# Revit family: Elite_OX_Standard
name_source: partatom
category: Windows
revit_build: Autodesk Revit 2014 (Build: 20130308_1515(x64)
units: mm (PartAtom-declared; Revit-internal decimal feet)

## types (108) — shared parameters
Centered In Wall = Yes
Custom Sash Width Left = 600 mm
Default Sill Height = 800 mm
Description = Elite Sliding Window OX
Equal Sash Width = Yes
Frame Thickness = 70 mm
Glass Type = Glass
Limit Sash Height Max = 1800 mm  [stored 5.90551 ft]
Limit Sash Height Min = 300 mm
Limit Sash Width Max = 1500 mm  [stored 4.92126 ft]
Limit Sash Width Min = 300 mm
Limit Window Height Max = 1883 mm
Limit Window Height Min = 383 mm  [stored 1.25656 ft]
Limit Window Width Min = 594 mm
Manufacturer = Crealco
Model = Elite Sliding Window OX
Rough Width = 3 mm  [stored 0.00984252 ft]
Sash Frame Seal = 3 mm  [stored 0.00984252 ft]
Sash Side Spacing = 1 mm  [stored 0.00328084 ft]
Wall Closure = By host
zero-valued in all types: Custom Frame Offset From Exterior

## per-type parameters (varying)
| type | Area Left Sash Glazing | Area Right Sash Glazing | Custom Windload | Custom Window Height | Custom Window Width | Glazing Thickness | Height | Inside Heavy Duty Interlocker | Interlocker Configuration | Limit Sash Width Left Max | Limit Sash Width Left Min | Limit Window Width Max | Max Pane Area | Outside Heavy Duty Interlocker | Sash Height | Sash Width Left | Sash Width Right | Standard Interlocker | Width | Windload Design |
| Elite-0906OX-1000Pa | 0.16 m² | 0.16 m² | 1000 mm  [stored 3.28084 ft] | 590 mm  [stored 1.9357 ft] | 890 mm  [stored 2.91995 ft] | 4 mm  [stored 0.0131234 ft] | 590 mm  [stored 1.9357 ft] | No | 0 mm  [stored 0 ft] | 596 mm | 300 mm | 2994 mm | 0.16 m² | No | 507 mm | 448 mm | 448 mm | Yes | 890 mm  [stored 2.91995 ft] | 1000 mm  [stored 3.28084 ft] |
| Elite-0906OX-1500Pa | 0.16 m² | 0.16 m² | 1500 mm  [stored 4.92126 ft] | 590 mm  [stored 1.9357 ft] | 890 mm  [stored 2.91995 ft] | 4 mm  [stored 0.0131234 ft] | 590 mm  [stored 1.9357 ft] | No | 0 mm  [stored 0 ft] | 596 mm | 300 mm | 2994 mm | 0.16 m² | No | 507 mm | 448 mm | 448 mm | Yes | 890 mm  [stored 2.91995 ft] | 1500 mm  [stored 4.92126 ft] |
| Elite-0906OX-2000Pa | 0.16 m² | 0.16 m² | 2000 mm  [stored 6.56168 ft] | 590 mm  [stored 1.9357 ft] | 890 mm  [stored 2.91995 ft] | 4 mm  [stored 0.0131234 ft] | 590 mm  [stored 1.9357 ft] | No | 0 mm  [stored 0 ft] | 596 mm | 300 mm | 2994 mm | 0.16 m² | No | 507 mm | 448 mm | 448 mm | Yes | 890 mm  [stored 2.91995 ft] | 2000 mm  [stored 6.56168 ft] |
| Elite-1206OX-1000Pa | 0.22 m² | 0.22 m² | 1000 mm  [stored 3.28084 ft] | 590 mm  [stored 1.9357 ft] | 1190 mm  [stored 3.9042 ft] | 4 mm  [stored 0.0131234 ft] | 590 mm  [stored 1.9357 ft] | No | 0 mm  [stored 0 ft] | 896 mm | 300 mm | 2994 mm | 0.22 m² | No | 507 mm | 598 mm | 598 mm | Yes | 1190 mm  [stored 3.9042 ft] | 1000 mm  [stored 3.28084 ft] |
| Elite-1206OX-1500Pa | 0.22 m² | 0.22 m² | 1500 mm  [stored 4.92126 ft] | 590 mm  [stored 1.9357 ft] | 1190 mm  [stored 3.9042 ft] | 4 mm  [stored 0.0131234 ft] | 590 mm  [stored 1.9357 ft] | No | 0 mm  [stored 0 ft] | 896 mm | 300 mm | 2994 mm | 0.22 m² | No | 507 mm | 598 mm | 598 mm | Yes | 1190 mm  [stored 3.9042 ft] | 1500 mm  [stored 4.92126 ft] |
| Elite-1206OX-2000Pa | 0.22 m² | 0.22 m² | 2000 mm  [stored 6.56168 ft] | 590 mm  [stored 1.9357 ft] | 1190 mm  [stored 3.9042 ft] | 4 mm  [stored 0.0131234 ft] | 590 mm  [stored 1.9357 ft] | No | 0 mm  [stored 0 ft] | 896 mm | 300 mm | 2994 mm | 0.22 m² | No | 507 mm | 598 mm | 598 mm | Yes | 1190 mm  [stored 3.9042 ft] | 2000 mm  [stored 6.56168 ft] |
| Elite-1506OX-1000Pa | 0.28 m² | 0.28 m² | 1000 mm  [stored 3.28084 ft] | 590 mm  [stored 1.9357 ft] | 1490 mm  [stored 4.88845 ft] | 4 mm  [stored 0.0131234 ft] | 590 mm  [stored 1.9357 ft] | No | 0 mm  [stored 0 ft] | 1196 mm | 300 mm | 2994 mm | 0.28 m² | No | 507 mm | 748 mm | 748 mm | Yes | 1490 mm  [stored 4.88845 ft] | 1000 mm  [stored 3.28084 ft] |
| Elite-1506OX-1500Pa | 0.28 m² | 0.28 m² | 1500 mm  [stored 4.92126 ft] | 590 mm  [stored 1.9357 ft] | 1490 mm  [stored 4.88845 ft] | 4 mm  [stored 0.0131234 ft] | 590 mm  [stored 1.9357 ft] | No | 0 mm  [stored 0 ft] | 1196 mm | 300 mm | 2994 mm | 0.28 m² | No | 507 mm | 748 mm | 748 mm | Yes | 1490 mm  [stored 4.88845 ft] | 1500 mm  [stored 4.92126 ft] |
| Elite-1506OX-2000Pa | 0.28 m² | 0.28 m² | 2000 mm  [stored 6.56168 ft] | 590 mm  [stored 1.9357 ft] | 1490 mm  [stored 4.88845 ft] | 4 mm  [stored 0.0131234 ft] | 590 mm  [stored 1.9357 ft] | No | 0 mm  [stored 0 ft] | 1196 mm | 300 mm | 2994 mm | 0.28 m² | No | 507 mm | 748 mm | 748 mm | Yes | 1490 mm  [stored 4.88845 ft] | 2000 mm  [stored 6.56168 ft] |
| Elite-1806OX-1000Pa | 0.35 m² | 0.35 m² | 1000 mm  [stored 3.28084 ft] | 590 mm  [stored 1.9357 ft] | 1790 mm  [stored 5.8727 ft] | 4 mm  [stored 0.0131234 ft] | 590 mm  [stored 1.9357 ft] | No | 0 mm  [stored 0 ft] | 1496 mm | 300 mm | 2994 mm | 0.35 m² | No | 507 mm | 898 mm | 898 mm | Yes | 1790 mm  [stored 5.8727 ft] | 1000 mm  [stored 3.28084 ft] |
| Elite-1806OX-1500Pa | 0.35 m² | 0.35 m² | 1500 mm  [stored 4.92126 ft] | 590 mm  [stored 1.9357 ft] | 1790 mm  [stored 5.8727 ft] | 4 mm  [stored 0.0131234 ft] | 590 mm  [stored 1.9357 ft] | No | 0 mm  [stored 0 ft] | 1496 mm | 300 mm | 2994 mm | 0.35 m² | No | 507 mm | 898 mm | 898 mm | Yes | 1790 mm  [stored 5.8727 ft] | 1500 mm  [stored 4.92126 ft] |
| Elite-1806OX-2000Pa | 0.35 m² | 0.35 m² | 2000 mm  [stored 6.56168 ft] | 590 mm  [stored 1.9357 ft] | 1790 mm  [stored 5.8727 ft] | 4 mm  [stored 0.0131234 ft] | 590 mm  [stored 1.9357 ft] | No | 0 mm  [stored 0 ft] | 1496 mm | 300 mm | 2994 mm | 0.35 m² | No | 507 mm | 898 mm | 898 mm | Yes | 1790 mm  [stored 5.8727 ft] | 2000 mm  [stored 6.56168 ft] |
| Elite-2106OX-1000Pa | 0.41 m² | 0.41 m² | 1000 mm  [stored 3.28084 ft] | 590 mm  [stored 1.9357 ft] | 2090 mm | 4 mm  [stored 0.0131234 ft] | 590 mm  [stored 1.9357 ft] | No | 0 mm  [stored 0 ft] | 1500 mm  [stored 4.92126 ft] | 596 mm | 2994 mm | 0.41 m² | No | 507 mm | 1048 mm | 1048 mm | Yes | 2090 mm | 1000 mm  [stored 3.28084 ft] |
| Elite-2106OX-1500Pa | 0.41 m² | 0.41 m² | 1500 mm  [stored 4.92126 ft] | 590 mm  [stored 1.9357 ft] | 2090 mm | 4 mm  [stored 0.0131234 ft] | 590 mm  [stored 1.9357 ft] | No | 0 mm  [stored 0 ft] | 1500 mm  [stored 4.92126 ft] | 596 mm | 2994 mm | 0.41 m² | No | 507 mm | 1048 mm | 1048 mm | Yes | 2090 mm | 1500 mm  [stored 4.92126 ft] |
| Elite-2106OX-2000Pa | 0.41 m² | 0.41 m² | 2000 mm  [stored 6.56168 ft] | 590 mm  [stored 1.9357 ft] | 2090 mm | 4 mm  [stored 0.0131234 ft] | 590 mm  [stored 1.9357 ft] | No | 0 mm  [stored 0 ft] | 1500 mm  [stored 4.92126 ft] | 596 mm | 2994 mm | 0.41 m² | No | 507 mm | 1048 mm | 1048 mm | Yes | 2090 mm | 2000 mm  [stored 6.56168 ft] |
| Elite-2406OX-1000Pa | 0.47 m² | 0.47 m² | 1000 mm  [stored 3.28084 ft] | 590 mm  [stored 1.9357 ft] | 2390 mm | 4 mm  [stored 0.0131234 ft] | 590 mm  [stored 1.9357 ft] | No | 0 mm  [stored 0 ft] | 1500 mm  [stored 4.92126 ft] | 896 mm | 2994 mm | 0.47 m² | No | 507 mm | 1198 mm | 1198 mm | Yes | 2390 mm | 1000 mm  [stored 3.28084 ft] |
| Elite-2406OX-1500Pa | 0.47 m² | 0.47 m² | 1500 mm  [stored 4.92126 ft] | 590 mm  [stored 1.9357 ft] | 2390 mm | 4 mm  [stored 0.0131234 ft] | 590 mm  [stored 1.9357 ft] | No | 0 mm  [stored 0 ft] | 1500 mm  [stored 4.92126 ft] | 896 mm | 2994 mm | 0.47 m² | No | 507 mm | 1198 mm | 1198 mm | Yes | 2390 mm | 1500 mm  [stored 4.92126 ft] |
| Elite-2406OX-2000Pa | 0.47 m² | 0.47 m² | 2000 mm  [stored 6.56168 ft] | 590 mm  [stored 1.9357 ft] | 2390 mm | 4 mm  [stored 0.0131234 ft] | 590 mm  [stored 1.9357 ft] | No | 0 mm  [stored 0 ft] | 1500 mm  [stored 4.92126 ft] | 896 mm | 2994 mm | 0.47 m² | No | 507 mm | 1198 mm | 1198 mm | Yes | 2390 mm | 2000 mm  [stored 6.56168 ft] |
| Elite-2706OX-1000Pa | 0.53 m² | 0.53 m² | 1000 mm  [stored 3.28084 ft] | 590 mm  [stored 1.9357 ft] | 2690 mm | 4 mm  [stored 0.0131234 ft] | 590 mm  [stored 1.9357 ft] | No | 0 mm  [stored 0 ft] | 1500 mm  [stored 4.92126 ft] | 1196 mm | 2994 mm | 0.53 m² | No | 507 mm | 1348 mm | 1348 mm | Yes | 2690 mm | 1000 mm  [stored 3.28084 ft] |
| Elite-2706OX-1500Pa | 0.53 m² | 0.53 m² | 1500 mm  [stored 4.92126 ft] | 590 mm  [stored 1.9357 ft] | 2690 mm | 4 mm  [stored 0.0131234 ft] | 590 mm  [stored 1.9357 ft] | No | 0 mm  [stored 0 ft] | 1500 mm  [stored 4.92126 ft] | 1196 mm | 2994 mm | 0.53 m² | No | 507 mm | 1348 mm | 1348 mm | Yes | 2690 mm | 1500 mm  [stored 4.92126 ft] |
| Elite-2706OX-2000Pa | 0.53 m² | 0.53 m² | 2000 mm  [stored 6.56168 ft] | 590 mm  [stored 1.9357 ft] | 2690 mm | 4 mm  [stored 0.0131234 ft] | 590 mm  [stored 1.9357 ft] | No | 0 mm  [stored 0 ft] | 1500 mm  [stored 4.92126 ft] | 1196 mm | 2994 mm | 0.53 m² | No | 507 mm | 1348 mm | 1348 mm | Yes | 2690 mm | 2000 mm  [stored 6.56168 ft] |
| Elite-3006OX-1000Pa | 0.6 m² | 0.6 m² | 1000 mm  [stored 3.28084 ft] | 590 mm  [stored 1.9357 ft] | 2990 mm | 4 mm  [stored 0.0131234 ft] | 590 mm  [stored 1.9357 ft] | No | 0 mm  [stored 0 ft] | 1500 mm  [stored 4.92126 ft] | 1496 mm | 2994 mm | 0.6 m² | No | 507 mm | 1498 mm | 1498 mm | Yes | 2990 mm | 1000 mm  [stored 3.28084 ft] |
| Elite-3006OX-1500Pa | 0.6 m² | 0.6 m² | 1500 mm  [stored 4.92126 ft] | 590 mm  [stored 1.9357 ft] | 2990 mm | 4 mm  [stored 0.0131234 ft] | 590 mm  [stored 1.9357 ft] | No | 0 mm  [stored 0 ft] | 1500 mm  [stored 4.92126 ft] | 1496 mm | 2994 mm | 0.6 m² | No | 507 mm | 1498 mm | 1498 mm | Yes | 2990 mm | 1500 mm  [stored 4.92126 ft] |
| Elite-3006OX-2000Pa | 0.6 m² | 0.6 m² | 2000 mm  [stored 6.56168 ft] | 590 mm  [stored 1.9357 ft] | 2990 mm | 4 mm  [stored 0.0131234 ft] | 590 mm  [stored 1.9357 ft] | No | 0 mm  [stored 0 ft] | 1500 mm  [stored 4.92126 ft] | 1496 mm | 2994 mm | 0.6 m² | No | 507 mm | 1498 mm | 1498 mm | Yes | 2990 mm | 2000 mm  [stored 6.56168 ft] |
| Elite-0909OX-1000Pa | 0.28 m² | 0.28 m² | 1000 mm  [stored 3.28084 ft] | 890 mm  [stored 2.91995 ft] | 890 mm  [stored 2.91995 ft] | 4 mm  [stored 0.0131234 ft] | 890 mm  [stored 2.91995 ft] | No | 0 mm  [stored 0 ft] | 596 mm | 300 mm | 2994 mm | 0.28 m² | No | 807 mm  [stored 2.64764 ft] | 448 mm | 448 mm | Yes | 890 mm  [stored 2.91995 ft] | 1000 mm  [stored 3.28084 ft] |
| Elite-0909OX-1500Pa | 0.28 m² | 0.28 m² | 1500 mm  [stored 4.92126 ft] | 890 mm  [stored 2.91995 ft] | 890 mm  [stored 2.91995 ft] | 4 mm  [stored 0.0131234 ft] | 890 mm  [stored 2.91995 ft] | No | 0 mm  [stored 0 ft] | 596 mm | 300 mm | 2994 mm | 0.28 m² | No | 807 mm  [stored 2.64764 ft] | 448 mm | 448 mm | Yes | 890 mm  [stored 2.91995 ft] | 1500 mm  [stored 4.92126 ft] |
| Elite-0909OX-2000Pa | 0.28 m² | 0.28 m² | 2000 mm  [stored 6.56168 ft] | 890 mm  [stored 2.91995 ft] | 890 mm  [stored 2.91995 ft] | 4 mm  [stored 0.0131234 ft] | 890 mm  [stored 2.91995 ft] | No | 0 mm  [stored 0 ft] | 596 mm | 300 mm | 2994 mm | 0.28 m² | No | 807 mm  [stored 2.64764 ft] | 448 mm | 448 mm | Yes | 890 mm  [stored 2.91995 ft] | 2000 mm  [stored 6.56168 ft] |
| Elite-1209OX-1000Pa | 0.38 m² | 0.38 m² | 1000 mm  [stored 3.28084 ft] | 890 mm  [stored 2.91995 ft] | 1190 mm  [stored 3.9042 ft] | 4 mm  [stored 0.0131234 ft] | 890 mm  [stored 2.91995 ft] | No | 0 mm  [stored 0 ft] | 896 mm | 300 mm | 2994 mm | 0.38 m² | No | 807 mm  [stored 2.64764 ft] | 598 mm | 598 mm | Yes | 1190 mm  [stored 3.9042 ft] | 1000 mm  [stored 3.28084 ft] |
| Elite-1209OX-1500Pa | 0.38 m² | 0.38 m² | 1500 mm  [stored 4.92126 ft] | 890 mm  [stored 2.91995 ft] | 1190 mm  [stored 3.9042 ft] | 4 mm  [stored 0.0131234 ft] | 890 mm  [stored 2.91995 ft] | No | 0 mm  [stored 0 ft] | 896 mm | 300 mm | 2994 mm | 0.38 m² | No | 807 mm  [stored 2.64764 ft] | 598 mm | 598 mm | Yes | 1190 mm  [stored 3.9042 ft] | 1500 mm  [stored 4.92126 ft] |
| Elite-1209OX-2000Pa | 0.38 m² | 0.38 m² | 2000 mm  [stored 6.56168 ft] | 890 mm  [stored 2.91995 ft] | 1190 mm  [stored 3.9042 ft] | 4 mm  [stored 0.0131234 ft] | 890 mm  [stored 2.91995 ft] | No | 0 mm  [stored 0 ft] | 896 mm | 300 mm | 2994 mm | 0.38 m² | No | 807 mm  [stored 2.64764 ft] | 598 mm | 598 mm | Yes | 1190 mm  [stored 3.9042 ft] | 2000 mm  [stored 6.56168 ft] |
| Elite-1509OX-1000Pa | 0.49 m² | 0.49 m² | 1000 mm  [stored 3.28084 ft] | 890 mm  [stored 2.91995 ft] | 1490 mm  [stored 4.88845 ft] | 4 mm  [stored 0.0131234 ft] | 890 mm  [stored 2.91995 ft] | No | 0 mm  [stored 0 ft] | 1196 mm | 300 mm | 2994 mm | 0.49 m² | No | 807 mm  [stored 2.64764 ft] | 748 mm | 748 mm | Yes | 1490 mm  [stored 4.88845 ft] | 1000 mm  [stored 3.28084 ft] |
| Elite-1509OX-1500Pa | 0.49 m² | 0.49 m² | 1500 mm  [stored 4.92126 ft] | 890 mm  [stored 2.91995 ft] | 1490 mm  [stored 4.88845 ft] | 4 mm  [stored 0.0131234 ft] | 890 mm  [stored 2.91995 ft] | No | 0 mm  [stored 0 ft] | 1196 mm | 300 mm | 2994 mm | 0.49 m² | No | 807 mm  [stored 2.64764 ft] | 748 mm | 748 mm | Yes | 1490 mm  [stored 4.88845 ft] | 1500 mm  [stored 4.92126 ft] |
| Elite-1509OX-2000Pa | 0.49 m² | 0.49 m² | 2000 mm  [stored 6.56168 ft] | 890 mm  [stored 2.91995 ft] | 1490 mm  [stored 4.88845 ft] | 4 mm  [stored 0.0131234 ft] | 890 mm  [stored 2.91995 ft] | No | 0 mm  [stored 0 ft] | 1196 mm | 300 mm | 2994 mm | 0.49 m² | No | 807 mm  [stored 2.64764 ft] | 748 mm | 748 mm | Yes | 1490 mm  [stored 4.88845 ft] | 2000 mm  [stored 6.56168 ft] |
| Elite-1809OX-1000Pa | 0.6 m² | 0.6 m² | 1000 mm  [stored 3.28084 ft] | 890 mm  [stored 2.91995 ft] | 1790 mm  [stored 5.8727 ft] | 4 mm  [stored 0.0131234 ft] | 890 mm  [stored 2.91995 ft] | No | 0 mm  [stored 0 ft] | 1496 mm | 300 mm | 2994 mm | 0.6 m² | No | 807 mm  [stored 2.64764 ft] | 898 mm | 898 mm | Yes | 1790 mm  [stored 5.8727 ft] | 1000 mm  [stored 3.28084 ft] |
| Elite-1809OX-1500Pa | 0.6 m² | 0.6 m² | 1500 mm  [stored 4.92126 ft] | 890 mm  [stored 2.91995 ft] | 1790 mm  [stored 5.8727 ft] | 4 mm  [stored 0.0131234 ft] | 890 mm  [stored 2.91995 ft] | No | 0 mm  [stored 0 ft] | 1496 mm | 300 mm | 2994 mm | 0.6 m² | No | 807 mm  [stored 2.64764 ft] | 898 mm | 898 mm | Yes | 1790 mm  [stored 5.8727 ft] | 1500 mm  [stored 4.92126 ft] |
| Elite-1809OX-2000Pa | 0.6 m² | 0.6 m² | 2000 mm  [stored 6.56168 ft] | 890 mm  [stored 2.91995 ft] | 1790 mm  [stored 5.8727 ft] | 4 mm  [stored 0.0131234 ft] | 890 mm  [stored 2.91995 ft] | No | 0 mm  [stored 0 ft] | 1496 mm | 300 mm | 2994 mm | 0.6 m² | No | 807 mm  [stored 2.64764 ft] | 898 mm | 898 mm | Yes | 1790 mm  [stored 5.8727 ft] | 2000 mm  [stored 6.56168 ft] |
| Elite-2109OX-1000Pa | 0.7 m² | 0.7 m² | 1000 mm  [stored 3.28084 ft] | 890 mm  [stored 2.91995 ft] | 2090 mm | 4 mm  [stored 0.0131234 ft] | 890 mm  [stored 2.91995 ft] | No | 0 mm  [stored 0 ft] | 1500 mm  [stored 4.92126 ft] | 596 mm | 2994 mm | 0.7 m² | No | 807 mm  [stored 2.64764 ft] | 1048 mm | 1048 mm | Yes | 2090 mm | 1000 mm  [stored 3.28084 ft] |
| Elite-2109OX-1500Pa | 0.7 m² | 0.7 m² | 1500 mm  [stored 4.92126 ft] | 890 mm  [stored 2.91995 ft] | 2090 mm | 4 mm  [stored 0.0131234 ft] | 890 mm  [stored 2.91995 ft] | No | 0 mm  [stored 0 ft] | 1500 mm  [stored 4.92126 ft] | 596 mm | 2994 mm | 0.7 m² | No | 807 mm  [stored 2.64764 ft] | 1048 mm | 1048 mm | Yes | 2090 mm | 1500 mm  [stored 4.92126 ft] |
| Elite-2109OX-2000Pa | 0.7 m² | 0.7 m² | 2000 mm  [stored 6.56168 ft] | 890 mm  [stored 2.91995 ft] | 2090 mm | 4 mm  [stored 0.0131234 ft] | 890 mm  [stored 2.91995 ft] | No | 0 mm  [stored 0 ft] | 1500 mm  [stored 4.92126 ft] | 596 mm | 2994 mm | 0.7 m² | No | 807 mm  [stored 2.64764 ft] | 1048 mm | 1048 mm | Yes | 2090 mm | 2000 mm  [stored 6.56168 ft] |
| Elite-2409OX-1000Pa | 0.81 m² | 0.81 m² | 1000 mm  [stored 3.28084 ft] | 890 mm  [stored 2.91995 ft] | 2390 mm | 4 mm  [stored 0.0131234 ft] | 890 mm  [stored 2.91995 ft] | No | 0 mm  [stored 0 ft] | 1500 mm  [stored 4.92126 ft] | 896 mm | 2994 mm | 0.81 m² | No | 807 mm  [stored 2.64764 ft] | 1198 mm | 1198 mm | Yes | 2390 mm | 1000 mm  [stored 3.28084 ft] |
| Elite-2409OX-1500Pa | 0.81 m² | 0.81 m² | 1500 mm  [stored 4.92126 ft] | 890 mm  [stored 2.91995 ft] | 2390 mm | 4 mm  [stored 0.0131234 ft] | 890 mm  [stored 2.91995 ft] | No | 0 mm  [stored 0 ft] | 1500 mm  [stored 4.92126 ft] | 896 mm | 2994 mm | 0.81 m² | No | 807 mm  [stored 2.64764 ft] | 1198 mm | 1198 mm | Yes | 2390 mm | 1500 mm  [stored 4.92126 ft] |
| Elite-2409OX-2000Pa | 0.81 m² | 0.81 m² | 2000 mm  [stored 6.56168 ft] | 890 mm  [stored 2.91995 ft] | 2390 mm | 4 mm  [stored 0.0131234 ft] | 890 mm  [stored 2.91995 ft] | No | 0 mm  [stored 0 ft] | 1500 mm  [stored 4.92126 ft] | 896 mm | 2994 mm | 0.81 m² | No | 807 mm  [stored 2.64764 ft] | 1198 mm | 1198 mm | Yes | 2390 mm | 2000 mm  [stored 6.56168 ft] |
| Elite-2709OX-1000Pa | 0.92 m² | 0.92 m² | 1000 mm  [stored 3.28084 ft] | 890 mm  [stored 2.91995 ft] | 2690 mm | 4 mm  [stored 0.0131234 ft] | 890 mm  [stored 2.91995 ft] | No | 0 mm  [stored 0 ft] | 1500 mm  [stored 4.92126 ft] | 1196 mm | 2994 mm | 0.92 m² | No | 807 mm  [stored 2.64764 ft] | 1348 mm | 1348 mm | Yes | 2690 mm | 1000 mm  [stored 3.28084 ft] |
| Elite-2709OX-1500Pa | 0.92 m² | 0.92 m² | 1500 mm  [stored 4.92126 ft] | 890 mm  [stored 2.91995 ft] | 2690 mm | 4 mm  [stored 0.0131234 ft] | 890 mm  [stored 2.91995 ft] | No | 0 mm  [stored 0 ft] | 1500 mm  [stored 4.92126 ft] | 1196 mm | 2994 mm | 0.92 m² | No | 807 mm  [stored 2.64764 ft] | 1348 mm | 1348 mm | Yes | 2690 mm | 1500 mm  [stored 4.92126 ft] |
| Elite-2709OX-2000Pa | 0.92 m² | 0.92 m² | 2000 mm  [stored 6.56168 ft] | 890 mm  [stored 2.91995 ft] | 2690 mm | 4 mm  [stored 0.0131234 ft] | 890 mm  [stored 2.91995 ft] | No | 0 mm  [stored 0 ft] | 1500 mm  [stored 4.92126 ft] | 1196 mm | 2994 mm | 0.92 m² | No | 807 mm  [stored 2.64764 ft] | 1348 mm | 1348 mm | Yes | 2690 mm | 2000 mm  [stored 6.56168 ft] |
| Elite-3009OX-1000Pa | 1.03 m² | 1.03 m² | 1000 mm  [stored 3.28084 ft] | 890 mm  [stored 2.91995 ft] | 2990 mm | 4 mm  [stored 0.0131234 ft] | 890 mm  [stored 2.91995 ft] | No | 0 mm  [stored 0 ft] | 1500 mm  [stored 4.92126 ft] | 1496 mm | 2994 mm | 1.03 m² | No | 807 mm  [stored 2.64764 ft] | 1498 mm | 1498 mm | Yes | 2990 mm | 1000 mm  [stored 3.28084 ft] |
| Elite-3009OX-1500Pa | 1.03 m² | 1.03 m² | 1500 mm  [stored 4.92126 ft] | 890 mm  [stored 2.91995 ft] | 2990 mm | 4 mm  [stored 0.0131234 ft] | 890 mm  [stored 2.91995 ft] | No | 0 mm  [stored 0 ft] | 1500 mm  [stored 4.92126 ft] | 1496 mm | 2994 mm | 1.03 m² | No | 807 mm  [stored 2.64764 ft] | 1498 mm | 1498 mm | Yes | 2990 mm | 1500 mm  [stored 4.92126 ft] |
| Elite-3009OX-2000Pa | 1.03 m² | 1.03 m² | 2000 mm  [stored 6.56168 ft] | 890 mm  [stored 2.91995 ft] | 2990 mm | 4 mm  [stored 0.0131234 ft] | 890 mm  [stored 2.91995 ft] | No | 0 mm  [stored 0 ft] | 1500 mm  [stored 4.92126 ft] | 1496 mm | 2994 mm | 1.03 m² | No | 807 mm  [stored 2.64764 ft] | 1498 mm | 1498 mm | Yes | 2990 mm | 2000 mm  [stored 6.56168 ft] |
| Elite-0912OX-1000Pa | 0.39 m² | 0.39 m² | 1000 mm  [stored 3.28084 ft] | 1190 mm  [stored 3.9042 ft] | 890 mm  [stored 2.91995 ft] | 4 mm  [stored 0.0131234 ft] | 1190 mm  [stored 3.9042 ft] | No | 0 mm  [stored 0 ft] | 596 mm | 300 mm | 2994 mm | 0.39 m² | No | 1107 mm  [stored 3.63189 ft] | 448 mm | 448 mm | Yes | 890 mm  [stored 2.91995 ft] | 1000 mm  [stored 3.28084 ft] |
| Elite-0912OX-1500Pa | 0.39 m² | 0.39 m² | 1500 mm  [stored 4.92126 ft] | 1190 mm  [stored 3.9042 ft] | 890 mm  [stored 2.91995 ft] | 4 mm  [stored 0.0131234 ft] | 1190 mm  [stored 3.9042 ft] | No | 0 mm  [stored 0 ft] | 596 mm | 300 mm | 2994 mm | 0.39 m² | No | 1107 mm  [stored 3.63189 ft] | 448 mm | 448 mm | Yes | 890 mm  [stored 2.91995 ft] | 1500 mm  [stored 4.92126 ft] |
| Elite-0912OX-2000Pa | 0.39 m² | 0.39 m² | 2000 mm  [stored 6.56168 ft] | 1190 mm  [stored 3.9042 ft] | 890 mm  [stored 2.91995 ft] | 4 mm  [stored 0.0131234 ft] | 1190 mm  [stored 3.9042 ft] | No | 0 mm  [stored 0 ft] | 596 mm | 300 mm | 2994 mm | 0.39 m² | No | 1107 mm  [stored 3.63189 ft] | 448 mm | 448 mm | Yes | 890 mm  [stored 2.91995 ft] | 2000 mm  [stored 6.56168 ft] |
| Elite-1212OX-1000Pa | 0.54 m² | 0.54 m² | 1000 mm  [stored 3.28084 ft] | 1190 mm  [stored 3.9042 ft] | 1190 mm  [stored 3.9042 ft] | 4 mm  [stored 0.0131234 ft] | 1190 mm  [stored 3.9042 ft] | No | 0 mm  [stored 0 ft] | 896 mm | 300 mm | 2994 mm | 0.54 m² | No | 1107 mm  [stored 3.63189 ft] | 598 mm | 598 mm | Yes | 1190 mm  [stored 3.9042 ft] | 1000 mm  [stored 3.28084 ft] |
| Elite-1212OX-1500Pa | 0.54 m² | 0.54 m² | 1500 mm  [stored 4.92126 ft] | 1190 mm  [stored 3.9042 ft] | 1190 mm  [stored 3.9042 ft] | 4 mm  [stored 0.0131234 ft] | 1190 mm  [stored 3.9042 ft] | No | 0 mm  [stored 0 ft] | 896 mm | 300 mm | 2994 mm | 0.54 m² | No | 1107 mm  [stored 3.63189 ft] | 598 mm | 598 mm | Yes | 1190 mm  [stored 3.9042 ft] | 1500 mm  [stored 4.92126 ft] |
| Elite-1212OX-2000Pa | 0.54 m² | 0.54 m² | 2000 mm  [stored 6.56168 ft] | 1190 mm  [stored 3.9042 ft] | 1190 mm  [stored 3.9042 ft] | 4 mm  [stored 0.0131234 ft] | 1190 mm  [stored 3.9042 ft] | Yes | 1 mm  [stored 0.00328084 ft] | 896 mm | 300 mm | 2994 mm | 0.54 m² | No | 1107 mm  [stored 3.63189 ft] | 598 mm | 598 mm | No | 1190 mm  [stored 3.9042 ft] | 2000 mm  [stored 6.56168 ft] |
| Elite-1512OX-1000Pa | 0.7 m² | 0.7 m² | 1000 mm  [stored 3.28084 ft] | 1190 mm  [stored 3.9042 ft] | 1490 mm  [stored 4.88845 ft] | 4 mm  [stored 0.0131234 ft] | 1190 mm  [stored 3.9042 ft] | No | 0 mm  [stored 0 ft] | 1196 mm | 300 mm | 2994 mm | 0.7 m² | No | 1107 mm  [stored 3.63189 ft] | 748 mm | 748 mm | Yes | 1490 mm  [stored 4.88845 ft] | 1000 mm  [stored 3.28084 ft] |
| Elite-1512OX-1500Pa | 0.7 m² | 0.7 m² | 1500 mm  [stored 4.92126 ft] | 1190 mm  [stored 3.9042 ft] | 1490 mm  [stored 4.88845 ft] | 4 mm  [stored 0.0131234 ft] | 1190 mm  [stored 3.9042 ft] | Yes | 1 mm  [stored 0.00328084 ft] | 1196 mm | 300 mm | 2994 mm | 0.7 m² | No | 1107 mm  [stored 3.63189 ft] | 748 mm | 748 mm | No | 1490 mm  [stored 4.88845 ft] | 1500 mm  [stored 4.92126 ft] |
| Elite-1512OX-2000Pa | 0.7 m² | 0.7 m² | 2000 mm  [stored 6.56168 ft] | 1190 mm  [stored 3.9042 ft] | 1490 mm  [stored 4.88845 ft] | 4 mm  [stored 0.0131234 ft] | 1190 mm  [stored 3.9042 ft] | Yes | 1 mm  [stored 0.00328084 ft] | 1196 mm | 300 mm | 2994 mm | 0.7 m² | No | 1107 mm  [stored 3.63189 ft] | 748 mm | 748 mm | No | 1490 mm  [stored 4.88845 ft] | 2000 mm  [stored 6.56168 ft] |
| Elite-1812OX-1000Pa | 0.85 m² | 0.85 m² | 1000 mm  [stored 3.28084 ft] | 1190 mm  [stored 3.9042 ft] | 1790 mm  [stored 5.8727 ft] | 4 mm  [stored 0.0131234 ft] | 1190 mm  [stored 3.9042 ft] | No | 0 mm  [stored 0 ft] | 1496 mm | 300 mm | 2994 mm | 0.85 m² | No | 1107 mm  [stored 3.63189 ft] | 898 mm | 898 mm | Yes | 1790 mm  [stored 5.8727 ft] | 1000 mm  [stored 3.28084 ft] |
| Elite-1812OX-1500Pa | 0.85 m² | 0.85 m² | 1500 mm  [stored 4.92126 ft] | 1190 mm  [stored 3.9042 ft] | 1790 mm  [stored 5.8727 ft] | 4 mm  [stored 0.0131234 ft] | 1190 mm  [stored 3.9042 ft] | Yes | 1 mm  [stored 0.00328084 ft] | 1496 mm | 300 mm | 2994 mm | 0.85 m² | No | 1107 mm  [stored 3.63189 ft] | 898 mm | 898 mm | No | 1790 mm  [stored 5.8727 ft] | 1500 mm  [stored 4.92126 ft] |
| Elite-1812OX-2000Pa | 0.85 m² | 0.85 m² | 2000 mm  [stored 6.56168 ft] | 1190 mm  [stored 3.9042 ft] | 1790 mm  [stored 5.8727 ft] | 4 mm  [stored 0.0131234 ft] | 1190 mm  [stored 3.9042 ft] | Yes | 1 mm  [stored 0.00328084 ft] | 1496 mm | 300 mm | 2994 mm | 0.85 m² | No | 1107 mm  [stored 3.63189 ft] | 898 mm | 898 mm | No | 1790 mm  [stored 5.8727 ft] | 2000 mm  [stored 6.56168 ft] |
| Elite-2112OX-1000Pa | 1 m² | 1 m² | 1000 mm  [stored 3.28084 ft] | 1190 mm  [stored 3.9042 ft] | 2090 mm | 4 mm  [stored 0.0131234 ft] | 1190 mm  [stored 3.9042 ft] | No | 0 mm  [stored 0 ft] | 1500 mm  [stored 4.92126 ft] | 596 mm | 2994 mm | 1 m² | No | 1107 mm  [stored 3.63189 ft] | 1048 mm | 1048 mm | Yes | 2090 mm | 1000 mm  [stored 3.28084 ft] |
| Elite-2112OX-1500Pa | 1 m² | 1 m² | 1500 mm  [stored 4.92126 ft] | 1190 mm  [stored 3.9042 ft] | 2090 mm | 4 mm  [stored 0.0131234 ft] | 1190 mm  [stored 3.9042 ft] | Yes | 1 mm  [stored 0.00328084 ft] | 1500 mm  [stored 4.92126 ft] | 596 mm | 2994 mm | 1 m² | No | 1107 mm  [stored 3.63189 ft] | 1048 mm | 1048 mm | No | 2090 mm | 1500 mm  [stored 4.92126 ft] |
| Elite-2112OX-2000Pa | 1 m² | 1 m² | 2000 mm  [stored 6.56168 ft] | 1190 mm  [stored 3.9042 ft] | 2090 mm | 4 mm  [stored 0.0131234 ft] | 1190 mm  [stored 3.9042 ft] | Yes | 1 mm  [stored 0.00328084 ft] | 1500 mm  [stored 4.92126 ft] | 596 mm | 2994 mm | 1 m² | No | 1107 mm  [stored 3.63189 ft] | 1048 mm | 1048 mm | No | 2090 mm | 2000 mm  [stored 6.56168 ft] |
| Elite-2412OX-1000Pa | 1.15 m² | 1.15 m² | 1000 mm  [stored 3.28084 ft] | 1190 mm  [stored 3.9042 ft] | 2390 mm | 4 mm  [stored 0.0131234 ft] | 1190 mm  [stored 3.9042 ft] | No | 0 mm  [stored 0 ft] | 1500 mm  [stored 4.92126 ft] | 896 mm | 2994 mm | 1.15 m² | No | 1107 mm  [stored 3.63189 ft] | 1198 mm | 1198 mm | Yes | 2390 mm | 1000 mm  [stored 3.28084 ft] |
| Elite-2412OX-1500Pa | 1.15 m² | 1.15 m² | 1500 mm  [stored 4.92126 ft] | 1190 mm  [stored 3.9042 ft] | 2390 mm | 4 mm  [stored 0.0131234 ft] | 1190 mm  [stored 3.9042 ft] | Yes | 1 mm  [stored 0.00328084 ft] | 1500 mm  [stored 4.92126 ft] | 896 mm | 2994 mm | 1.15 m² | No | 1107 mm  [stored 3.63189 ft] | 1198 mm | 1198 mm | No | 2390 mm | 1500 mm  [stored 4.92126 ft] |
| Elite-2412OX-2000Pa | 1.15 m² | 1.15 m² | 2000 mm  [stored 6.56168 ft] | 1190 mm  [stored 3.9042 ft] | 2390 mm | 4 mm  [stored 0.0131234 ft] | 1190 mm  [stored 3.9042 ft] | Yes | 1 mm  [stored 0.00328084 ft] | 1500 mm  [stored 4.92126 ft] | 896 mm | 2994 mm | 1.15 m² | No | 1107 mm  [stored 3.63189 ft] | 1198 mm | 1198 mm | No | 2390 mm | 2000 mm  [stored 6.56168 ft] |
| Elite-2712OX-1000Pa | 1.31 m² | 1.31 m² | 1000 mm  [stored 3.28084 ft] | 1190 mm  [stored 3.9042 ft] | 2690 mm | 4 mm  [stored 0.0131234 ft] | 1190 mm  [stored 3.9042 ft] | No | 0 mm  [stored 0 ft] | 1500 mm  [stored 4.92126 ft] | 1196 mm | 2994 mm | 1.31 m² | No | 1107 mm  [stored 3.63189 ft] | 1348 mm | 1348 mm | Yes | 2690 mm | 1000 mm  [stored 3.28084 ft] |
| Elite-2712OX-1500Pa | 1.31 m² | 1.31 m² | 1500 mm  [stored 4.92126 ft] | 1190 mm  [stored 3.9042 ft] | 2690 mm | 4 mm  [stored 0.0131234 ft] | 1190 mm  [stored 3.9042 ft] | Yes | 1 mm  [stored 0.00328084 ft] | 1500 mm  [stored 4.92126 ft] | 1196 mm | 2994 mm | 1.31 m² | No | 1107 mm  [stored 3.63189 ft] | 1348 mm | 1348 mm | No | 2690 mm | 1500 mm  [stored 4.92126 ft] |
| Elite-2712OX-2000Pa | 1.31 m² | 1.31 m² | 2000 mm  [stored 6.56168 ft] | 1190 mm  [stored 3.9042 ft] | 2690 mm | 4 mm  [stored 0.0131234 ft] | 1190 mm  [stored 3.9042 ft] | Yes | 1 mm  [stored 0.00328084 ft] | 1500 mm  [stored 4.92126 ft] | 1196 mm | 2994 mm | 1.31 m² | No | 1107 mm  [stored 3.63189 ft] | 1348 mm | 1348 mm | No | 2690 mm | 2000 mm  [stored 6.56168 ft] |
| Elite-3012OX-1000Pa | 1.46 m² | 1.46 m² | 1000 mm  [stored 3.28084 ft] | 1190 mm  [stored 3.9042 ft] | 2990 mm | 4 mm  [stored 0.0131234 ft] | 1190 mm  [stored 3.9042 ft] | Yes | 1 mm  [stored 0.00328084 ft] | 1500 mm  [stored 4.92126 ft] | 1496 mm | 2994 mm | 1.46 m² | No | 1107 mm  [stored 3.63189 ft] | 1498 mm | 1498 mm | No | 2990 mm | 1000 mm  [stored 3.28084 ft] |
| Elite-3012OX-1500Pa | 1.46 m² | 1.46 m² | 1500 mm  [stored 4.92126 ft] | 1190 mm  [stored 3.9042 ft] | 2990 mm | 4 mm  [stored 0.0131234 ft] | 1190 mm  [stored 3.9042 ft] | Yes | 1 mm  [stored 0.00328084 ft] | 1500 mm  [stored 4.92126 ft] | 1496 mm | 2994 mm | 1.46 m² | No | 1107 mm  [stored 3.63189 ft] | 1498 mm | 1498 mm | No | 2990 mm | 1500 mm  [stored 4.92126 ft] |
| Elite-3012OX-2000Pa | 1.46 m² | 1.46 m² | 2000 mm  [stored 6.56168 ft] | 1190 mm  [stored 3.9042 ft] | 2990 mm | 4 mm  [stored 0.0131234 ft] | 1190 mm  [stored 3.9042 ft] | Yes | 1 mm  [stored 0.00328084 ft] | 1500 mm  [stored 4.92126 ft] | 1496 mm | 2994 mm | 1.46 m² | No | 1107 mm  [stored 3.63189 ft] | 1498 mm | 1498 mm | No | 2990 mm | 2000 mm  [stored 6.56168 ft] |
| Elite-0915OX-1000Pa | 0.51 m² | 0.51 m² | 1000 mm  [stored 3.28084 ft] | 1490 mm  [stored 4.88845 ft] | 890 mm  [stored 2.91995 ft] | 4 mm  [stored 0.0131234 ft] | 1490 mm  [stored 4.88845 ft] | No | 0 mm  [stored 0 ft] | 596 mm | 300 mm | 2994 mm | 0.51 m² | No | 1407 mm  [stored 4.61614 ft] | 448 mm | 448 mm | Yes | 890 mm  [stored 2.91995 ft] | 1000 mm  [stored 3.28084 ft] |
| Elite-0915OX-1500Pa | 0.51 m² | 0.51 m² | 1500 mm  [stored 4.92126 ft] | 1490 mm  [stored 4.88845 ft] | 890 mm  [stored 2.91995 ft] | 4 mm  [stored 0.0131234 ft] | 1490 mm  [stored 4.88845 ft] | Yes | 1 mm  [stored 0.00328084 ft] | 596 mm | 300 mm | 2994 mm | 0.51 m² | No | 1407 mm  [stored 4.61614 ft] | 448 mm | 448 mm | No | 890 mm  [stored 2.91995 ft] | 1500 mm  [stored 4.92126 ft] |
| Elite-0915OX-2000Pa | 0.51 m² | 0.51 m² | 2000 mm  [stored 6.56168 ft] | 1490 mm  [stored 4.88845 ft] | 890 mm  [stored 2.91995 ft] | 4 mm  [stored 0.0131234 ft] | 1490 mm  [stored 4.88845 ft] | Yes | 1 mm  [stored 0.00328084 ft] | 596 mm | 300 mm | 2994 mm | 0.51 m² | No | 1407 mm  [stored 4.61614 ft] | 448 mm | 448 mm | No | 890 mm  [stored 2.91995 ft] | 2000 mm  [stored 6.56168 ft] |
| Elite-1215OX-1000Pa | 0.7 m² | 0.7 m² | 1000 mm  [stored 3.28084 ft] | 1490 mm  [stored 4.88845 ft] | 1190 mm  [stored 3.9042 ft] | 4 mm  [stored 0.0131234 ft] | 1490 mm  [stored 4.88845 ft] | Yes | 1 mm  [stored 0.00328084 ft] | 896 mm | 300 mm | 2994 mm | 0.7 m² | No | 1407 mm  [stored 4.61614 ft] | 598 mm | 598 mm | No | 1190 mm  [stored 3.9042 ft] | 1000 mm  [stored 3.28084 ft] |
| Elite-1215OX-1500Pa | 0.7 m² | 0.7 m² | 1500 mm  [stored 4.92126 ft] | 1490 mm  [stored 4.88845 ft] | 1190 mm  [stored 3.9042 ft] | 4 mm  [stored 0.0131234 ft] | 1490 mm  [stored 4.88845 ft] | Yes | 1 mm  [stored 0.00328084 ft] | 896 mm | 300 mm | 2994 mm | 0.7 m² | No | 1407 mm  [stored 4.61614 ft] | 598 mm | 598 mm | No | 1190 mm  [stored 3.9042 ft] | 1500 mm  [stored 4.92126 ft] |
| Elite-1215OX-2000Pa | 0.7 m² | 0.7 m² | 2000 mm  [stored 6.56168 ft] | 1490 mm  [stored 4.88845 ft] | 1190 mm  [stored 3.9042 ft] | 4 mm  [stored 0.0131234 ft] | 1490 mm  [stored 4.88845 ft] | Yes | 1 mm  [stored 0.00328084 ft] | 896 mm | 300 mm | 2994 mm | 0.7 m² | No | 1407 mm  [stored 4.61614 ft] | 598 mm | 598 mm | No | 1190 mm  [stored 3.9042 ft] | 2000 mm  [stored 6.56168 ft] |
| Elite-1515OX-1000Pa | 0.9 m² | 0.9 m² | 1000 mm  [stored 3.28084 ft] | 1490 mm  [stored 4.88845 ft] | 1490 mm  [stored 4.88845 ft] | 4 mm  [stored 0.0131234 ft] | 1490 mm  [stored 4.88845 ft] | Yes | 1 mm  [stored 0.00328084 ft] | 1196 mm | 300 mm | 2994 mm | 0.9 m² | No | 1407 mm  [stored 4.61614 ft] | 748 mm | 748 mm | No | 1490 mm  [stored 4.88845 ft] | 1000 mm  [stored 3.28084 ft] |
| Elite-1515OX-1500Pa | 0.9 m² | 0.9 m² | 1500 mm  [stored 4.92126 ft] | 1490 mm  [stored 4.88845 ft] | 1490 mm  [stored 4.88845 ft] | 4 mm  [stored 0.0131234 ft] | 1490 mm  [stored 4.88845 ft] | Yes | 1 mm  [stored 0.00328084 ft] | 1196 mm | 300 mm | 2994 mm | 0.9 m² | No | 1407 mm  [stored 4.61614 ft] | 748 mm | 748 mm | No | 1490 mm  [stored 4.88845 ft] | 1500 mm  [stored 4.92126 ft] |
| Elite-1515OX-2000Pa | 0.9 m² | 0.9 m² | 2000 mm  [stored 6.56168 ft] | 1490 mm  [stored 4.88845 ft] | 1490 mm  [stored 4.88845 ft] | 4 mm  [stored 0.0131234 ft] | 1490 mm  [stored 4.88845 ft] | Yes | 2 mm  [stored 0.00656168 ft] | 1196 mm | 300 mm | 2994 mm | 0.9 m² | Yes | 1407 mm  [stored 4.61614 ft] | 748 mm | 748 mm | No | 1490 mm  [stored 4.88845 ft] | 2000 mm  [stored 6.56168 ft] |
| Elite-1815OX-1000Pa | 1.1 m² | 1.1 m² | 1000 mm  [stored 3.28084 ft] | 1490 mm  [stored 4.88845 ft] | 1790 mm  [stored 5.8727 ft] | 4 mm  [stored 0.0131234 ft] | 1490 mm  [stored 4.88845 ft] | Yes | 1 mm  [stored 0.00328084 ft] | 1496 mm | 300 mm | 2994 mm | 1.1 m² | No | 1407 mm  [stored 4.61614 ft] | 898 mm | 898 mm | No | 1790 mm  [stored 5.8727 ft] | 1000 mm  [stored 3.28084 ft] |
| Elite-1815OX-1500Pa | 1.1 m² | 1.1 m² | 1500 mm  [stored 4.92126 ft] | 1490 mm  [stored 4.88845 ft] | 1790 mm  [stored 5.8727 ft] | 4 mm  [stored 0.0131234 ft] | 1490 mm  [stored 4.88845 ft] | Yes | 1 mm  [stored 0.00328084 ft] | 1496 mm | 300 mm | 2994 mm | 1.1 m² | No | 1407 mm  [stored 4.61614 ft] | 898 mm | 898 mm | No | 1790 mm  [stored 5.8727 ft] | 1500 mm  [stored 4.92126 ft] |
| Elite-1815OX-2000Pa | 1.1 m² | 1.1 m² | 2000 mm  [stored 6.56168 ft] | 1490 mm  [stored 4.88845 ft] | 1790 mm  [stored 5.8727 ft] | 4 mm  [stored 0.0131234 ft] | 1490 mm  [stored 4.88845 ft] | Yes | 2 mm  [stored 0.00656168 ft] | 1496 mm | 300 mm | 2994 mm | 1.1 m² | Yes | 1407 mm  [stored 4.61614 ft] | 898 mm | 898 mm | No | 1790 mm  [stored 5.8727 ft] | 2000 mm  [stored 6.56168 ft] |
| Elite-2115OX-1000Pa | 1.3 m² | 1.3 m² | 1000 mm  [stored 3.28084 ft] | 1490 mm  [stored 4.88845 ft] | 2090 mm | 4 mm  [stored 0.0131234 ft] | 1490 mm  [stored 4.88845 ft] | Yes | 1 mm  [stored 0.00328084 ft] | 1500 mm  [stored 4.92126 ft] | 596 mm | 2994 mm | 1.3 m² | No | 1407 mm  [stored 4.61614 ft] | 1048 mm | 1048 mm | No | 2090 mm | 1000 mm  [stored 3.28084 ft] |
| Elite-2115OX-1500Pa | 1.3 m² | 1.3 m² | 1500 mm  [stored 4.92126 ft] | 1490 mm  [stored 4.88845 ft] | 2090 mm | 4 mm  [stored 0.0131234 ft] | 1490 mm  [stored 4.88845 ft] | Yes | 2 mm  [stored 0.00656168 ft] | 1500 mm  [stored 4.92126 ft] | 596 mm | 2994 mm | 1.3 m² | Yes | 1407 mm  [stored 4.61614 ft] | 1048 mm | 1048 mm | No | 2090 mm | 1500 mm  [stored 4.92126 ft] |
| Elite-2115OX-2000Pa | 1.3 m² | 1.3 m² | 2000 mm  [stored 6.56168 ft] | 1490 mm  [stored 4.88845 ft] | 2090 mm | 4 mm  [stored 0.0131234 ft] | 1490 mm  [stored 4.88845 ft] | Yes | 2 mm  [stored 0.00656168 ft] | 1500 mm  [stored 4.92126 ft] | 596 mm | 2994 mm | 1.3 m² | Yes | 1407 mm  [stored 4.61614 ft] | 1048 mm | 1048 mm | No | 2090 mm | 2000 mm  [stored 6.56168 ft] |
| Elite-2415OX-1000Pa | 1.49 m² | 1.49 m² | 1000 mm  [stored 3.28084 ft] | 1490 mm  [stored 4.88845 ft] | 2390 mm | 4 mm  [stored 0.0131234 ft] | 1490 mm  [stored 4.88845 ft] | Yes | 1 mm  [stored 0.00328084 ft] | 1500 mm  [stored 4.92126 ft] | 896 mm | 2994 mm | 1.49 m² | No | 1407 mm  [stored 4.61614 ft] | 1198 mm | 1198 mm | No | 2390 mm | 1000 mm  [stored 3.28084 ft] |
| Elite-2415OX-1500Pa | 1.49 m² | 1.49 m² | 1500 mm  [stored 4.92126 ft] | 1490 mm  [stored 4.88845 ft] | 2390 mm | 4 mm  [stored 0.0131234 ft] | 1490 mm  [stored 4.88845 ft] | Yes | 2 mm  [stored 0.00656168 ft] | 1500 mm  [stored 4.92126 ft] | 896 mm | 2994 mm | 1.49 m² | Yes | 1407 mm  [stored 4.61614 ft] | 1198 mm | 1198 mm | No | 2390 mm | 1500 mm  [stored 4.92126 ft] |
| Elite-2415OX-2000Pa | 1.49 m² | 1.49 m² | 2000 mm  [stored 6.56168 ft] | 1490 mm  [stored 4.88845 ft] | 2390 mm | 4 mm  [stored 0.0131234 ft] | 1490 mm  [stored 4.88845 ft] | Yes | 2 mm  [stored 0.00656168 ft] | 1500 mm  [stored 4.92126 ft] | 896 mm | 2994 mm | 1.49 m² | Yes | 1407 mm  [stored 4.61614 ft] | 1198 mm | 1198 mm | No | 2390 mm | 2000 mm  [stored 6.56168 ft] |
| Elite-2715OX-1000Pa | 1.69 m² | 1.69 m² | 1000 mm  [stored 3.28084 ft] | 1490 mm  [stored 4.88845 ft] | 2690 mm | 5 mm  [stored 0.0164042 ft] | 1490 mm  [stored 4.88845 ft] | Yes | 1 mm  [stored 0.00328084 ft] | 1500 mm  [stored 4.92126 ft] | 1196 mm | 2994 mm | 1.69 m² | No | 1407 mm  [stored 4.61614 ft] | 1348 mm | 1348 mm | No | 2690 mm | 1000 mm  [stored 3.28084 ft] |
| Elite-2715OX-1500Pa | 1.69 m² | 1.69 m² | 1500 mm  [stored 4.92126 ft] | 1490 mm  [stored 4.88845 ft] | 2690 mm | 5 mm  [stored 0.0164042 ft] | 1490 mm  [stored 4.88845 ft] | Yes | 2 mm  [stored 0.00656168 ft] | 1500 mm  [stored 4.92126 ft] | 1196 mm | 2994 mm | 1.69 m² | Yes | 1407 mm  [stored 4.61614 ft] | 1348 mm | 1348 mm | No | 2690 mm | 1500 mm  [stored 4.92126 ft] |
| Elite-2715OX-2000Pa | 1.69 m² | 1.69 m² | 2000 mm  [stored 6.56168 ft] | 1490 mm  [stored 4.88845 ft] | 2690 mm | 5 mm  [stored 0.0164042 ft] | 1490 mm  [stored 4.88845 ft] | Yes | 2 mm  [stored 0.00656168 ft] | 1500 mm  [stored 4.92126 ft] | 1196 mm | 2994 mm | 1.69 m² | Yes | 1407 mm  [stored 4.61614 ft] | 1348 mm | 1348 mm | No | 2690 mm | 2000 mm  [stored 6.56168 ft] |
| Elite-3015OX-1000Pa | 1.89 m² | 1.89 m² | 1000 mm  [stored 3.28084 ft] | 1490 mm  [stored 4.88845 ft] | 2990 mm | 5 mm  [stored 0.0164042 ft] | 1490 mm  [stored 4.88845 ft] | Yes | 1 mm  [stored 0.00328084 ft] | 1500 mm  [stored 4.92126 ft] | 1496 mm | 2994 mm | 1.89 m² | No | 1407 mm  [stored 4.61614 ft] | 1498 mm | 1498 mm | No | 2990 mm | 1000 mm  [stored 3.28084 ft] |
| Elite-3015OX-1500Pa | 1.89 m² | 1.89 m² | 1500 mm  [stored 4.92126 ft] | 1490 mm  [stored 4.88845 ft] | 2990 mm | 5 mm  [stored 0.0164042 ft] | 1490 mm  [stored 4.88845 ft] | Yes | 2 mm  [stored 0.00656168 ft] | 1500 mm  [stored 4.92126 ft] | 1496 mm | 2994 mm | 1.89 m² | Yes | 1407 mm  [stored 4.61614 ft] | 1498 mm | 1498 mm | No | 2990 mm | 1500 mm  [stored 4.92126 ft] |
| Elite-3015OX-2000Pa | 1.89 m² | 1.89 m² | 2000 mm  [stored 6.56168 ft] | 1490 mm  [stored 4.88845 ft] | 2990 mm | 5 mm  [stored 0.0164042 ft] | 1490 mm  [stored 4.88845 ft] | Yes | 2 mm  [stored 0.00656168 ft] | 1500 mm  [stored 4.92126 ft] | 1496 mm | 2994 mm | 1.89 m² | Yes | 1407 mm  [stored 4.61614 ft] | 1498 mm | 1498 mm | No | 2990 mm | 2000 mm  [stored 6.56168 ft] |
| Elite-0918OX-1000Pa | 0.62 m² | 0.62 m² | 1000 mm  [stored 3.28084 ft] | 1790 mm  [stored 5.8727 ft] | 890 mm  [stored 2.91995 ft] | 4 mm  [stored 0.0131234 ft] | 1790 mm  [stored 5.8727 ft] | Yes | 1 mm  [stored 0.00328084 ft] | 596 mm | 300 mm | 2994 mm | 0.62 m² | No | 1707 mm | 448 mm | 448 mm | No | 890 mm  [stored 2.91995 ft] | 1000 mm  [stored 3.28084 ft] |
| Elite-0918OX-1500Pa | 0.62 m² | 0.62 m² | 1500 mm  [stored 4.92126 ft] | 1790 mm  [stored 5.8727 ft] | 890 mm  [stored 2.91995 ft] | 4 mm  [stored 0.0131234 ft] | 1790 mm  [stored 5.8727 ft] | Yes | 1 mm  [stored 0.00328084 ft] | 596 mm | 300 mm | 1490 mm  [stored 4.88845 ft] | 0.62 m² | No | 1707 mm | 448 mm | 448 mm | No | 890 mm  [stored 2.91995 ft] | 1500 mm  [stored 4.92126 ft] |
| Elite-0918OX-2000Pa | 0.62 m² | 0.62 m² | 2000 mm  [stored 6.56168 ft] | 1790 mm  [stored 5.8727 ft] | 890 mm  [stored 2.91995 ft] | 4 mm  [stored 0.0131234 ft] | 1790 mm  [stored 5.8727 ft] | Yes | 2 mm  [stored 0.00656168 ft] | 596 mm | 300 mm | 890 mm  [stored 2.91995 ft] | 0.62 m² | Yes | 1707 mm | 448 mm | 448 mm | No | 890 mm  [stored 2.91995 ft] | 2000 mm  [stored 6.56168 ft] |
| Elite-1218OX-1000Pa | 0.87 m² | 0.87 m² | 1000 mm  [stored 3.28084 ft] | 1790 mm  [stored 5.8727 ft] | 1190 mm  [stored 3.9042 ft] | 4 mm  [stored 0.0131234 ft] | 1790 mm  [stored 5.8727 ft] | Yes | 1 mm  [stored 0.00328084 ft] | 896 mm | 300 mm | 2994 mm | 0.87 m² | No | 1707 mm | 598 mm | 598 mm | No | 1190 mm  [stored 3.9042 ft] | 1000 mm  [stored 3.28084 ft] |
| Elite-1218OX-1500Pa | 0.87 m² | 0.87 m² | 1500 mm  [stored 4.92126 ft] | 1790 mm  [stored 5.8727 ft] | 1190 mm  [stored 3.9042 ft] | 4 mm  [stored 0.0131234 ft] | 1790 mm  [stored 5.8727 ft] | Yes | 2 mm  [stored 0.00656168 ft] | 896 mm | 300 mm | 1490 mm  [stored 4.88845 ft] | 0.87 m² | Yes | 1707 mm | 598 mm | 598 mm | No | 1190 mm  [stored 3.9042 ft] | 1500 mm  [stored 4.92126 ft] |
| Elite-1518OX-1000Pa | 1.11 m² | 1.11 m² | 1000 mm  [stored 3.28084 ft] | 1790 mm  [stored 5.8727 ft] | 1490 mm  [stored 4.88845 ft] | 4 mm  [stored 0.0131234 ft] | 1790 mm  [stored 5.8727 ft] | Yes | 2 mm  [stored 0.00656168 ft] | 1196 mm | 300 mm | 2994 mm | 1.11 m² | Yes | 1707 mm | 748 mm | 748 mm | No | 1490 mm  [stored 4.88845 ft] | 1000 mm  [stored 3.28084 ft] |
| Elite-1518OX-1500Pa | 1.11 m² | 1.11 m² | 1500 mm  [stored 4.92126 ft] | 1790 mm  [stored 5.8727 ft] | 1490 mm  [stored 4.88845 ft] | 4 mm  [stored 0.0131234 ft] | 1790 mm  [stored 5.8727 ft] | Yes | 2 mm  [stored 0.00656168 ft] | 1196 mm | 300 mm | 1490 mm  [stored 4.88845 ft] | 1.11 m² | Yes | 1707 mm | 748 mm | 748 mm | No | 1490 mm  [stored 4.88845 ft] | 1500 mm  [stored 4.92126 ft] |
| Elite-1818OX-1000Pa | 1.35 m² | 1.35 m² | 1000 mm  [stored 3.28084 ft] | 1790 mm  [stored 5.8727 ft] | 1790 mm  [stored 5.8727 ft] | 4 mm  [stored 0.0131234 ft] | 1790 mm  [stored 5.8727 ft] | Yes | 2 mm  [stored 0.00656168 ft] | 1496 mm | 300 mm | 2994 mm | 1.35 m² | Yes | 1707 mm | 898 mm | 898 mm | No | 1790 mm  [stored 5.8727 ft] | 1000 mm  [stored 3.28084 ft] |
| Elite-2118OX-1000Pa | 1.59 m² | 1.59 m² | 1000 mm  [stored 3.28084 ft] | 1790 mm  [stored 5.8727 ft] | 2090 mm | 5 mm  [stored 0.0164042 ft] | 1790 mm  [stored 5.8727 ft] | Yes | 2 mm  [stored 0.00656168 ft] | 1500 mm  [stored 4.92126 ft] | 596 mm | 2994 mm | 1.59 m² | Yes | 1707 mm | 1048 mm | 1048 mm | No | 2090 mm | 1000 mm  [stored 3.28084 ft] |
| Elite-2418OX-1000Pa | 1.83 m² | 1.83 m² | 1000 mm  [stored 3.28084 ft] | 1790 mm  [stored 5.8727 ft] | 2390 mm | 5 mm  [stored 0.0164042 ft] | 1790 mm  [stored 5.8727 ft] | Yes | 2 mm  [stored 0.00656168 ft] | 1500 mm  [stored 4.92126 ft] | 896 mm | 2994 mm | 1.83 m² | Yes | 1707 mm | 1198 mm | 1198 mm | No | 2390 mm | 1000 mm  [stored 3.28084 ft] |
| Elite-2718OX-1000Pa | 2.08 m² | 2.08 m² | 1000 mm  [stored 3.28084 ft] | 1790 mm  [stored 5.8727 ft] | 2690 mm | 5 mm  [stored 0.0164042 ft] | 1790 mm  [stored 5.8727 ft] | Yes | 2 mm  [stored 0.00656168 ft] | 1500 mm  [stored 4.92126 ft] | 1196 mm | 2994 mm | 2.08 m² | Yes | 1707 mm | 1348 mm | 1348 mm | No | 2690 mm | 1000 mm  [stored 3.28084 ft] |
| Elite-3018OX-1000Pa | 2.32 m² | 2.32 m² | 1000 mm  [stored 3.28084 ft] | 1790 mm  [stored 5.8727 ft] | 2990 mm | 6 mm  [stored 0.019685 ft] | 1790 mm  [stored 5.8727 ft] | Yes | 2 mm  [stored 0.00656168 ft] | 1500 mm  [stored 4.92126 ft] | 1496 mm | 2994 mm | 2.32 m² | Yes | 1707 mm | 1498 mm | 1498 mm | No | 2990 mm | 1000 mm  [stored 3.28084 ft] |

note: [stored X ft] marks values corroborated as IEEE doubles in the binary element streams (Revit-internal decimal feet)

## geometry (parser evidence)
native form markers: Sweep x57
no freeform markers — native parametric forms only
